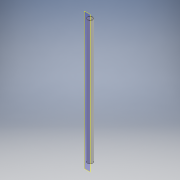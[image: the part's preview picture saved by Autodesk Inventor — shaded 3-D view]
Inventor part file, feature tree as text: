
AUTODESK INVENTOR PART (.ipt)
format: ipt  version: 2018 (Build 220112000, 112)  size: 93,696 bytes
history: native  units: mm
features: other x2, extrude x1, sketch x1
ambient origin geometry x8: Origin, YZ Plane, XZ Plane, XY Plane, X Axis, Y Axis, Z Axis, Center Point
bodies: Body1 (feature_tree)
feature tree (4):
  other  "ソリッド1"
  extrude  "押し出し1"  Depth=27.2mm
  other  "作業平面1"
  sketch  "スケッチ1"
